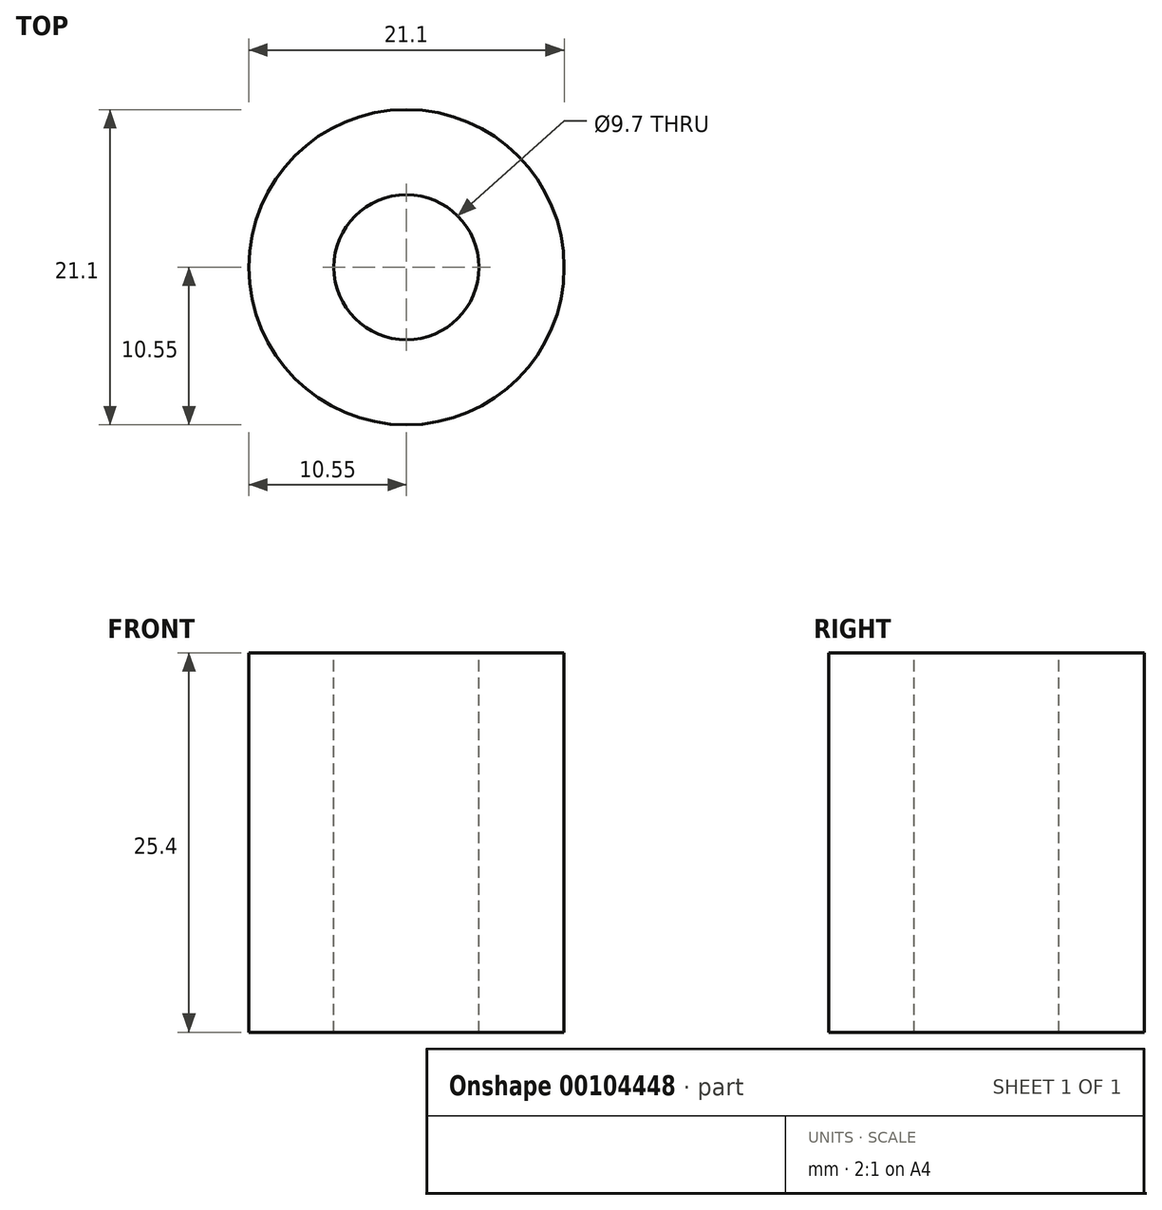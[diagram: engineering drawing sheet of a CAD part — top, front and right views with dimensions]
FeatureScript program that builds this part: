
annotation { "Feature Type Name" : "Feature", "Feature Type Description" : "" }
export const myFeature = defineFeature(function(context is Context, id is Id, definition is map)
    precondition{}
    {
        {
            var Q0;
            Q0=qCreatedBy(makeId("Front.planeOp"),FACE);
            var sketch = newSketch(context, id + "F0", { "sketchPlane" : qUnion([Q0])});
            skLineSegment(sketch, "E0", {"start": v(0, 0) * mm, "end": v(10.55, 0) * mm});
            skLineSegment(sketch, "E1", {"start": v(10.55, 0) * mm, "end": v(10.55, 25.4) * mm});
            skLineSegment(sketch, "E2", {"start": v(9.72, 25.4) * mm, "end": v(0, 25.4) * mm});
            skLineSegment(sketch, "E3", {"start": v(0, 25.4) * mm, "end": v(0, 0) * mm});
            skLineSegment(sketch, "E4", {"start": v(-0.3, 0.14) * mm, "end": v(10.55, 0) * mm});
            skLineSegment(sketch, "E5", {"start": v(10.55, 25.4) * mm, "end": v(0, 25.4) * mm});
            skSolve(sketch);
        }
        {
            var Q0;
            Q0 = qSketchRegion(id + "F0", true);
            var Q1;
            Q1=sQuery(id+"F0.wireOp",EDGE,"E3");
            revolve(context, id + "F1", {"entities" : qUnion([Q0]), "axis" : qUnion([Q1]), "revolveType" : RevolveType.FULL});
        }
        {
            var Q0;
            Q0=makeQuery(id+"F1.opRevolve","SWEPT_FACE",FACE,{"disambiguationData":[OSD([sQuery(id+"F0.wireOp",EDGE,"E5")])]});
            var sketch = newSketch(context, id + "F2", { "sketchPlane" : qUnion([Q0])});
            skCircle(sketch, "E6", {"center": v(0, 0) * mm, "radius": 4.85 * mm});
            skSolve(sketch);
        }
        {
            var Q0;
            Q0 = qSketchRegion(id + "F2", true);
            extrude(context, id + "F3", {"entities" : qUnion([Q0]), "operationType" : NewBodyOperationType.REMOVE, "oppositeDirection" : true, "depth" : 25.4 * mm});
        }
    });
